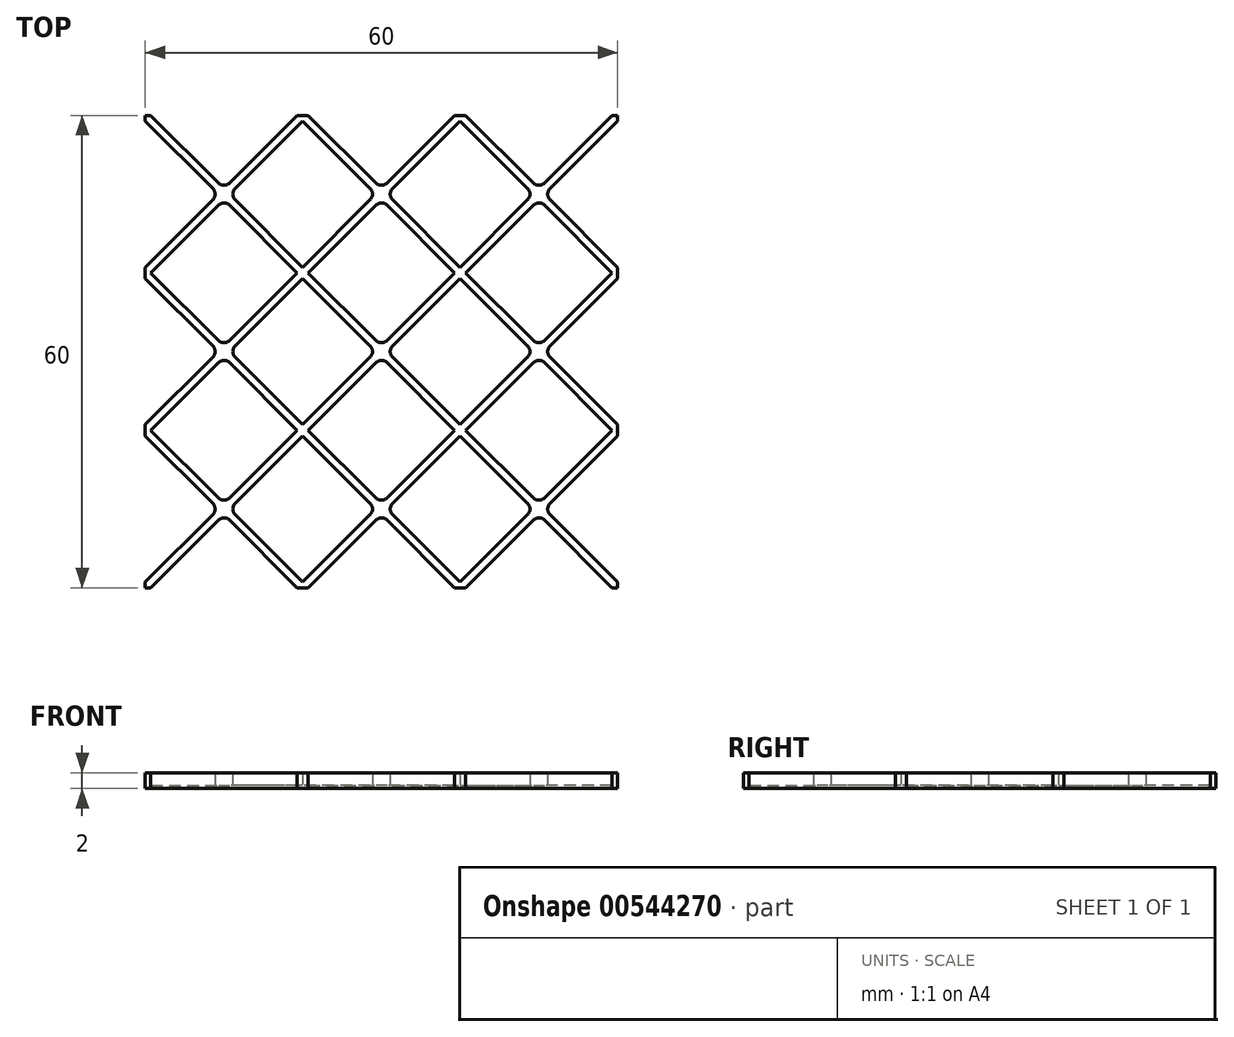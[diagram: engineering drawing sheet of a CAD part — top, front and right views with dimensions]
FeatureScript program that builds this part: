
annotation { "Feature Type Name" : "Feature", "Feature Type Description" : "" }
export const myFeature = defineFeature(function(context is Context, id is Id, definition is map)
    precondition{}
    {
        {
            var Q0;
            Q0=qCreatedBy(makeId("Top.planeOp"),FACE);
            var sketch = newSketch(context, id + "F0", { "sketchPlane" : qUnion([Q0])});
            skLineSegment(sketch, "E0.bottom", {"start": v(10, -10) * mm, "end": v(-10, -10) * mm, "construction": true});
            skLineSegment(sketch, "E0.top", {"start": v(10, 10) * mm, "end": v(-10, 10) * mm, "construction": true});
            skLineSegment(sketch, "E0.left", {"start": v(10, -10) * mm, "end": v(10, 10) * mm, "construction": true});
            skLineSegment(sketch, "E0.right", {"start": v(-10, -10) * mm, "end": v(-10, 10) * mm, "construction": true});
            skPoint(sketch, "E0.middle", {"position": v(0, 0) * mm});
            skLineSegment(sketch, "E1", {"start": v(-10, -10) * mm, "end": v(10, 10) * mm, "construction": true});
            skLineSegment(sketch, "E2", {"start": v(-10, 10) * mm, "end": v(10, -10) * mm, "construction": true});
            skArc(sketch, "E3.0.startCap", {"start": v(-10.35, 9.65) * mm, "mid": v(-10.35, 10.35) * mm, "end": v(-9.65, 10.35) * mm, "construction": true});
            skArc(sketch, "E3.0.endCap", {"start": v(10.35, -9.65) * mm, "mid": v(10.35, -10.35) * mm, "end": v(9.65, -10.35) * mm, "construction": true});
            skLineSegment(sketch, "E3.0.left", {"start": v(-9.65, 10.35) * mm, "end": v(-0.7, 1.41) * mm, "construction": true});
            skLineSegment(sketch, "E3.0.right", {"start": v(-10.35, 9.65) * mm, "end": v(-1.41, 0.7) * mm, "construction": true});
            skArc(sketch, "E3.1.startCap", {"start": v(-9.65, -10.35) * mm, "mid": v(-10.35, -10.35) * mm, "end": v(-10.35, -9.65) * mm, "construction": true});
            skArc(sketch, "E3.1.endCap", {"start": v(9.65, 10.35) * mm, "mid": v(10.35, 10.35) * mm, "end": v(10.35, 9.65) * mm, "construction": true});
            skLineSegment(sketch, "E3.1.left", {"start": v(-10.35, -9.65) * mm, "end": v(-1.41, -0.7) * mm, "construction": true});
            skLineSegment(sketch, "E3.1.right", {"start": v(-9.65, -10.35) * mm, "end": v(-0.7, -1.41) * mm, "construction": true});
            skPoint(sketch, "E4", {"position": v(0, -0.7) * mm});
            skPoint(sketch, "E5", {"position": v(-0.7, 0) * mm});
            skPoint(sketch, "E6", {"position": v(0, 0.7) * mm});
            skPoint(sketch, "E7", {"position": v(0.7, 0) * mm});
            skLineSegment(sketch, "E8", {"start": v(-0.7, 0) * mm, "end": v(-0.7, 0) * mm});
            skLineSegment(sketch, "E9", {"start": v(0.7, 1.41) * mm, "end": v(9.65, 10.35) * mm, "construction": true});
            skLineSegment(sketch, "E10", {"start": v(1.41, -0.7) * mm, "end": v(10.35, -9.65) * mm, "construction": true});
            skLineSegment(sketch, "E11", {"start": v(0, -0.7) * mm, "end": v(0.7, 0) * mm, "construction": true});
            skLineSegment(sketch, "E12", {"start": v(-0.7, 0) * mm, "end": v(0, 0.7) * mm, "construction": true});
            skLineSegment(sketch, "E13", {"start": v(0.7, -1.41) * mm, "end": v(9.65, -10.35) * mm, "construction": true});
            skLineSegment(sketch, "E14", {"start": v(1.41, 0.7) * mm, "end": v(10.35, 9.65) * mm, "construction": true});
            skLineSegment(sketch, "E15", {"start": v(0, 0.7) * mm, "end": v(0.7, 0) * mm, "construction": true});
            skLineSegment(sketch, "E16", {"start": v(-0.7, 0) * mm, "end": v(0, -0.7) * mm, "construction": true});
            skArc(sketch, "E17.filletArc", {"start": v(-1.41, -0.7) * mm, "mid": v(-1.12, 0) * mm, "end": v(-1.41, 0.7) * mm});
            skArc(sketch, "E18.filletArc", {"start": v(-0.7, 1.41) * mm, "mid": v(0, 1.12) * mm, "end": v(0.7, 1.41) * mm});
            skArc(sketch, "E19.filletArc", {"start": v(1.41, 0.7) * mm, "mid": v(1.12, 0) * mm, "end": v(1.41, -0.7) * mm});
            skArc(sketch, "E20.filletArc", {"start": v(0.7, -1.41) * mm, "mid": v(0, -1.12) * mm, "end": v(-0.7, -1.41) * mm});
            skPoint(sketch, "E21", {"position": v(9.3, 10) * mm});
            skPoint(sketch, "E22", {"position": v(10, 9.3) * mm});
            skPoint(sketch, "E23", {"position": v(10, -9.3) * mm});
            skPoint(sketch, "E24", {"position": v(-9.3, -10) * mm});
            skPoint(sketch, "E25", {"position": v(-10, -9.3) * mm});
            skPoint(sketch, "E26", {"position": v(-10, 9.3) * mm});
            skPoint(sketch, "E27", {"position": v(-9.3, 10) * mm});
            skPoint(sketch, "E28", {"position": v(9.3, -10) * mm});
            skLineSegment(sketch, "E29", {"start": v(-1.41, 0.7) * mm, "end": v(-10, 9.3) * mm});
            skLineSegment(sketch, "E30", {"start": v(-10, 9.3) * mm, "end": v(-10, 10) * mm});
            skLineSegment(sketch, "E31", {"start": v(-10, 10) * mm, "end": v(-9.3, 10) * mm});
            skLineSegment(sketch, "E32", {"start": v(-9.3, 10) * mm, "end": v(-0.7, 1.41) * mm});
            skLineSegment(sketch, "E33", {"start": v(0.7, 1.41) * mm, "end": v(9.3, 10) * mm});
            skLineSegment(sketch, "E34", {"start": v(9.3, 10) * mm, "end": v(10, 10) * mm});
            skLineSegment(sketch, "E35", {"start": v(10, 10) * mm, "end": v(10, 9.3) * mm});
            skLineSegment(sketch, "E36", {"start": v(10, 9.3) * mm, "end": v(1.41, 0.7) * mm});
            skLineSegment(sketch, "E37", {"start": v(1.41, -0.7) * mm, "end": v(10, -9.3) * mm});
            skLineSegment(sketch, "E38", {"start": v(10, -9.3) * mm, "end": v(10, -10) * mm});
            skLineSegment(sketch, "E39", {"start": v(10, -10) * mm, "end": v(9.3, -10) * mm});
            skLineSegment(sketch, "E40", {"start": v(9.3, -10) * mm, "end": v(0.7, -1.41) * mm});
            skLineSegment(sketch, "E41", {"start": v(-0.7, -1.41) * mm, "end": v(-9.3, -10) * mm});
            skLineSegment(sketch, "E42", {"start": v(-9.3, -10) * mm, "end": v(-10, -10) * mm});
            skLineSegment(sketch, "E43", {"start": v(-10, -10) * mm, "end": v(-10, -9.3) * mm});
            skLineSegment(sketch, "E44", {"start": v(-10, -9.3) * mm, "end": v(-1.41, -0.7) * mm});
            skLineSegment(sketch, "E45.0.1.0", {"start": v(-10.35, 29.65) * mm, "end": v(-1.41, 20.7) * mm, "construction": true});
            skLineSegment(sketch, "E45.0.1.1", {"start": v(-10, 10) * mm, "end": v(10, 30) * mm, "construction": true});
            skLineSegment(sketch, "E45.0.1.2", {"start": v(0, 20.7) * mm, "end": v(0.7, 20) * mm, "construction": true});
            skPoint(sketch, "E45.0.1.3", {"position": v(9.3, 30) * mm});
            skLineSegment(sketch, "E45.0.1.4", {"start": v(10, 10) * mm, "end": v(10, 30) * mm, "construction": true});
            skLineSegment(sketch, "E45.0.1.5", {"start": v(-10, 10) * mm, "end": v(-10, 30) * mm, "construction": true});
            skArc(sketch, "E45.0.1.6", {"start": v(-10.35, 29.65) * mm, "mid": v(-10.35, 30.35) * mm, "end": v(-9.65, 30.35) * mm, "construction": true});
            skPoint(sketch, "E45.0.1.7", {"position": v(-10, 29.3) * mm});
            skArc(sketch, "E45.0.1.8", {"start": v(10.35, 10.35) * mm, "mid": v(10.35, 9.65) * mm, "end": v(9.65, 9.65) * mm, "construction": true});
            skPoint(sketch, "E45.0.1.10", {"position": v(10, 29.3) * mm});
            skArc(sketch, "E45.0.1.11", {"start": v(1.41, 20.7) * mm, "mid": v(1.12, 20) * mm, "end": v(1.41, 19.3) * mm});
            skLineSegment(sketch, "E45.0.1.12", {"start": v(1.41, 19.3) * mm, "end": v(10.35, 10.35) * mm, "construction": true});
            skPoint(sketch, "E45.0.1.13", {"position": v(0, 20.7) * mm});
            skLineSegment(sketch, "E45.0.1.14", {"start": v(-10.35, 10.35) * mm, "end": v(-1.41, 19.3) * mm, "construction": true});
            skPoint(sketch, "E45.0.1.15", {"position": v(-9.3, 30) * mm});
            skArc(sketch, "E45.0.1.16", {"start": v(-0.7, 21.41) * mm, "mid": v(0, 21.12) * mm, "end": v(0.7, 21.41) * mm});
            skLineSegment(sketch, "E45.0.1.17", {"start": v(0, 19.3) * mm, "end": v(0.7, 20) * mm, "construction": true});
            skLineSegment(sketch, "E45.0.1.18", {"start": v(-0.7, 20) * mm, "end": v(0, 20.7) * mm, "construction": true});
            skLineSegment(sketch, "E45.0.1.19", {"start": v(10, 30) * mm, "end": v(-10, 30) * mm, "construction": true});
            skPoint(sketch, "E45.0.1.20", {"position": v(0, 20) * mm});
            skPoint(sketch, "E45.0.1.22", {"position": v(10, 10.7) * mm});
            skLineSegment(sketch, "E45.0.1.23", {"start": v(-9.65, 30.35) * mm, "end": v(-0.7, 21.41) * mm, "construction": true});
            skLineSegment(sketch, "E45.0.1.24", {"start": v(0.7, 21.41) * mm, "end": v(9.65, 30.35) * mm, "construction": true});
            skLineSegment(sketch, "E45.0.1.25", {"start": v(-10, 30) * mm, "end": v(10, 10) * mm, "construction": true});
            skArc(sketch, "E45.0.1.26", {"start": v(-9.65, 9.65) * mm, "mid": v(-10.35, 9.65) * mm, "end": v(-10.35, 10.35) * mm, "construction": true});
            skLineSegment(sketch, "E45.0.1.27", {"start": v(-0.7, 20) * mm, "end": v(0, 19.3) * mm, "construction": true});
            skArc(sketch, "E45.0.1.28", {"start": v(9.65, 30.35) * mm, "mid": v(10.35, 30.35) * mm, "end": v(10.35, 29.65) * mm, "construction": true});
            skLineSegment(sketch, "E45.0.1.29", {"start": v(-9.65, 9.65) * mm, "end": v(-0.7, 18.59) * mm, "construction": true});
            skPoint(sketch, "E45.0.1.30", {"position": v(0.7, 20) * mm});
            skArc(sketch, "E45.0.1.32", {"start": v(0.7, 18.59) * mm, "mid": v(0, 18.88) * mm, "end": v(-0.7, 18.59) * mm});
            skArc(sketch, "E45.0.1.33", {"start": v(-1.41, 19.3) * mm, "mid": v(-1.12, 20) * mm, "end": v(-1.41, 20.7) * mm});
            skPoint(sketch, "E45.0.1.34", {"position": v(0, 19.3) * mm});
            skLineSegment(sketch, "E45.0.1.35", {"start": v(1.41, 20.7) * mm, "end": v(10.35, 29.65) * mm, "construction": true});
            skPoint(sketch, "E45.0.1.36", {"position": v(-10, 10.7) * mm});
            skLineSegment(sketch, "E45.0.1.37", {"start": v(0.7, 18.59) * mm, "end": v(9.65, 9.65) * mm, "construction": true});
            skPoint(sketch, "E45.0.1.38", {"position": v(0, 19.3) * mm});
            skLineSegment(sketch, "E45.0.1.39", {"start": v(0.7, 21.41) * mm, "end": v(9.3, 30) * mm});
            skLineSegment(sketch, "E45.0.1.40", {"start": v(10, 10) * mm, "end": v(9.3, 10) * mm});
            skLineSegment(sketch, "E45.0.1.41", {"start": v(-10, 29.3) * mm, "end": v(-10, 30) * mm});
            skLineSegment(sketch, "E45.0.1.42", {"start": v(-9.3, 30) * mm, "end": v(-0.7, 21.41) * mm});
            skLineSegment(sketch, "E45.0.1.43", {"start": v(10, 29.3) * mm, "end": v(1.41, 20.7) * mm});
            skLineSegment(sketch, "E45.0.1.44", {"start": v(-10, 30) * mm, "end": v(-9.3, 30) * mm});
            skLineSegment(sketch, "E45.0.1.45", {"start": v(9.3, 10) * mm, "end": v(0.7, 18.59) * mm});
            skLineSegment(sketch, "E45.0.1.46", {"start": v(-9.3, 10) * mm, "end": v(-10, 10) * mm});
            skPoint(sketch, "E45.0.1.47", {"position": v(-0.7, 20) * mm});
            skLineSegment(sketch, "E45.0.1.48", {"start": v(10, 30) * mm, "end": v(10, 29.3) * mm});
            skPoint(sketch, "E45.0.1.49", {"position": v(0, 20.7) * mm});
            skLineSegment(sketch, "E45.0.1.50", {"start": v(-10, 10) * mm, "end": v(-10, 10.7) * mm});
            skLineSegment(sketch, "E45.0.1.51", {"start": v(10, 10.7) * mm, "end": v(10, 10) * mm});
            skLineSegment(sketch, "E45.0.1.52", {"start": v(1.41, 19.3) * mm, "end": v(10, 10.7) * mm});
            skPoint(sketch, "E45.0.1.53", {"position": v(0.7, 20) * mm});
            skLineSegment(sketch, "E45.0.1.54", {"start": v(-10, 10.7) * mm, "end": v(-1.41, 19.3) * mm});
            skLineSegment(sketch, "E45.0.1.55", {"start": v(-1.41, 20.7) * mm, "end": v(-10, 29.3) * mm});
            skLineSegment(sketch, "E45.0.1.56", {"start": v(-0.7, 18.59) * mm, "end": v(-9.3, 10) * mm});
            skLineSegment(sketch, "E45.0.1.57", {"start": v(9.3, 30) * mm, "end": v(10, 30) * mm});
            skPoint(sketch, "E45.0.1.58", {"position": v(-0.7, 20) * mm});
            skLineSegment(sketch, "E45.0.2.0", {"start": v(-10.35, 49.65) * mm, "end": v(-1.41, 40.7) * mm, "construction": true});
            skLineSegment(sketch, "E45.0.2.1", {"start": v(-10, 30) * mm, "end": v(10, 50) * mm, "construction": true});
            skLineSegment(sketch, "E45.0.2.2", {"start": v(0, 40.7) * mm, "end": v(0.7, 40) * mm, "construction": true});
            skPoint(sketch, "E45.0.2.3", {"position": v(9.3, 50) * mm});
            skLineSegment(sketch, "E45.0.2.4", {"start": v(10, 30) * mm, "end": v(10, 50) * mm, "construction": true});
            skLineSegment(sketch, "E45.0.2.5", {"start": v(-10, 30) * mm, "end": v(-10, 50) * mm, "construction": true});
            skArc(sketch, "E45.0.2.6", {"start": v(-10.35, 49.65) * mm, "mid": v(-10.35, 50.35) * mm, "end": v(-9.65, 50.35) * mm, "construction": true});
            skPoint(sketch, "E45.0.2.7", {"position": v(-10, 49.3) * mm});
            skArc(sketch, "E45.0.2.8", {"start": v(10.35, 30.35) * mm, "mid": v(10.35, 29.65) * mm, "end": v(9.65, 29.65) * mm, "construction": true});
            skPoint(sketch, "E45.0.2.9", {"position": v(9.3, 30) * mm});
            skPoint(sketch, "E45.0.2.10", {"position": v(10, 49.3) * mm});
            skArc(sketch, "E45.0.2.11", {"start": v(1.41, 40.7) * mm, "mid": v(1.12, 40) * mm, "end": v(1.41, 39.3) * mm});
            skLineSegment(sketch, "E45.0.2.12", {"start": v(1.41, 39.3) * mm, "end": v(10.35, 30.35) * mm, "construction": true});
            skPoint(sketch, "E45.0.2.13", {"position": v(0, 40.7) * mm});
            skLineSegment(sketch, "E45.0.2.14", {"start": v(-10.35, 30.35) * mm, "end": v(-1.41, 39.3) * mm, "construction": true});
            skPoint(sketch, "E45.0.2.15", {"position": v(-9.3, 50) * mm});
            skArc(sketch, "E45.0.2.16", {"start": v(-0.7, 41.41) * mm, "mid": v(0, 41.12) * mm, "end": v(0.7, 41.41) * mm});
            skLineSegment(sketch, "E45.0.2.17", {"start": v(0, 39.3) * mm, "end": v(0.7, 40) * mm, "construction": true});
            skLineSegment(sketch, "E45.0.2.18", {"start": v(-0.7, 40) * mm, "end": v(0, 40.7) * mm, "construction": true});
            skLineSegment(sketch, "E45.0.2.19", {"start": v(10, 50) * mm, "end": v(-10, 50) * mm, "construction": true});
            skPoint(sketch, "E45.0.2.20", {"position": v(0, 40) * mm});
            skLineSegment(sketch, "E45.0.2.21", {"start": v(10, 30) * mm, "end": v(-10, 30) * mm, "construction": true});
            skPoint(sketch, "E45.0.2.22", {"position": v(10, 30.7) * mm});
            skLineSegment(sketch, "E45.0.2.23", {"start": v(-9.65, 50.35) * mm, "end": v(-0.7, 41.41) * mm, "construction": true});
            skLineSegment(sketch, "E45.0.2.24", {"start": v(0.7, 41.41) * mm, "end": v(9.65, 50.35) * mm, "construction": true});
            skLineSegment(sketch, "E45.0.2.25", {"start": v(-10, 50) * mm, "end": v(10, 30) * mm, "construction": true});
            skArc(sketch, "E45.0.2.26", {"start": v(-9.65, 29.65) * mm, "mid": v(-10.35, 29.65) * mm, "end": v(-10.35, 30.35) * mm, "construction": true});
            skLineSegment(sketch, "E45.0.2.27", {"start": v(-0.7, 40) * mm, "end": v(0, 39.3) * mm, "construction": true});
            skArc(sketch, "E45.0.2.28", {"start": v(9.65, 50.35) * mm, "mid": v(10.35, 50.35) * mm, "end": v(10.35, 49.65) * mm, "construction": true});
            skLineSegment(sketch, "E45.0.2.29", {"start": v(-9.65, 29.65) * mm, "end": v(-0.7, 38.59) * mm, "construction": true});
            skPoint(sketch, "E45.0.2.30", {"position": v(0.7, 40) * mm});
            skPoint(sketch, "E45.0.2.31", {"position": v(-9.3, 30) * mm});
            skArc(sketch, "E45.0.2.32", {"start": v(0.7, 38.59) * mm, "mid": v(0, 38.88) * mm, "end": v(-0.7, 38.59) * mm});
            skArc(sketch, "E45.0.2.33", {"start": v(-1.41, 39.3) * mm, "mid": v(-1.12, 40) * mm, "end": v(-1.41, 40.7) * mm});
            skPoint(sketch, "E45.0.2.34", {"position": v(0, 39.3) * mm});
            skLineSegment(sketch, "E45.0.2.35", {"start": v(1.41, 40.7) * mm, "end": v(10.35, 49.65) * mm, "construction": true});
            skPoint(sketch, "E45.0.2.36", {"position": v(-10, 30.7) * mm});
            skLineSegment(sketch, "E45.0.2.37", {"start": v(0.7, 38.59) * mm, "end": v(9.65, 29.65) * mm, "construction": true});
            skPoint(sketch, "E45.0.2.38", {"position": v(0, 39.3) * mm});
            skLineSegment(sketch, "E45.0.2.39", {"start": v(0.7, 41.41) * mm, "end": v(9.3, 50) * mm});
            skLineSegment(sketch, "E45.0.2.40", {"start": v(10, 30) * mm, "end": v(9.3, 30) * mm});
            skLineSegment(sketch, "E45.0.2.41", {"start": v(-10, 49.3) * mm, "end": v(-10, 50) * mm});
            skLineSegment(sketch, "E45.0.2.42", {"start": v(-9.3, 50) * mm, "end": v(-0.7, 41.41) * mm});
            skLineSegment(sketch, "E45.0.2.43", {"start": v(10, 49.3) * mm, "end": v(1.41, 40.7) * mm});
            skLineSegment(sketch, "E45.0.2.44", {"start": v(-10, 50) * mm, "end": v(-9.3, 50) * mm});
            skLineSegment(sketch, "E45.0.2.45", {"start": v(9.3, 30) * mm, "end": v(0.7, 38.59) * mm});
            skLineSegment(sketch, "E45.0.2.46", {"start": v(-9.3, 30) * mm, "end": v(-10, 30) * mm});
            skPoint(sketch, "E45.0.2.47", {"position": v(-0.7, 40) * mm});
            skLineSegment(sketch, "E45.0.2.48", {"start": v(10, 50) * mm, "end": v(10, 49.3) * mm});
            skPoint(sketch, "E45.0.2.49", {"position": v(0, 40.7) * mm});
            skLineSegment(sketch, "E45.0.2.50", {"start": v(-10, 30) * mm, "end": v(-10, 30.7) * mm});
            skLineSegment(sketch, "E45.0.2.51", {"start": v(10, 30.7) * mm, "end": v(10, 30) * mm});
            skLineSegment(sketch, "E45.0.2.52", {"start": v(1.41, 39.3) * mm, "end": v(10, 30.7) * mm});
            skPoint(sketch, "E45.0.2.53", {"position": v(0.7, 40) * mm});
            skLineSegment(sketch, "E45.0.2.54", {"start": v(-10, 30.7) * mm, "end": v(-1.41, 39.3) * mm});
            skLineSegment(sketch, "E45.0.2.55", {"start": v(-1.41, 40.7) * mm, "end": v(-10, 49.3) * mm});
            skLineSegment(sketch, "E45.0.2.56", {"start": v(-0.7, 38.59) * mm, "end": v(-9.3, 30) * mm});
            skLineSegment(sketch, "E45.0.2.57", {"start": v(9.3, 50) * mm, "end": v(10, 50) * mm});
            skPoint(sketch, "E45.0.2.58", {"position": v(-0.7, 40) * mm});
            skLineSegment(sketch, "E45.1.0.0", {"start": v(9.65, 9.65) * mm, "end": v(18.59, 0.7) * mm, "construction": true});
            skLineSegment(sketch, "E45.1.0.1", {"start": v(10, -10) * mm, "end": v(30, 10) * mm, "construction": true});
            skLineSegment(sketch, "E45.1.0.2", {"start": v(20, 0.7) * mm, "end": v(20.7, 0) * mm, "construction": true});
            skPoint(sketch, "E45.1.0.3", {"position": v(29.3, 10) * mm});
            skLineSegment(sketch, "E45.1.0.4", {"start": v(30, -10) * mm, "end": v(30, 10) * mm, "construction": true});
            skArc(sketch, "E45.1.0.6", {"start": v(9.65, 9.65) * mm, "mid": v(9.65, 10.35) * mm, "end": v(10.35, 10.35) * mm, "construction": true});
            skArc(sketch, "E45.1.0.8", {"start": v(30.35, -9.65) * mm, "mid": v(30.35, -10.35) * mm, "end": v(29.65, -10.35) * mm, "construction": true});
            skPoint(sketch, "E45.1.0.9", {"position": v(29.3, -10) * mm});
            skPoint(sketch, "E45.1.0.10", {"position": v(30, 9.3) * mm});
            skArc(sketch, "E45.1.0.11", {"start": v(21.41, 0.7) * mm, "mid": v(21.12, 0) * mm, "end": v(21.41, -0.7) * mm});
            skLineSegment(sketch, "E45.1.0.12", {"start": v(21.41, -0.7) * mm, "end": v(30.35, -9.65) * mm, "construction": true});
            skPoint(sketch, "E45.1.0.13", {"position": v(20, 0.7) * mm});
            skLineSegment(sketch, "E45.1.0.14", {"start": v(9.65, -9.65) * mm, "end": v(18.59, -0.7) * mm, "construction": true});
            skPoint(sketch, "E45.1.0.15", {"position": v(10.7, 10) * mm});
            skArc(sketch, "E45.1.0.16", {"start": v(19.3, 1.41) * mm, "mid": v(20, 1.12) * mm, "end": v(20.7, 1.41) * mm});
            skLineSegment(sketch, "E45.1.0.17", {"start": v(20, -0.7) * mm, "end": v(20.7, 0) * mm, "construction": true});
            skLineSegment(sketch, "E45.1.0.18", {"start": v(19.3, 0) * mm, "end": v(20, 0.7) * mm, "construction": true});
            skLineSegment(sketch, "E45.1.0.19", {"start": v(30, 10) * mm, "end": v(10, 10) * mm, "construction": true});
            skPoint(sketch, "E45.1.0.20", {"position": v(20, 0) * mm});
            skLineSegment(sketch, "E45.1.0.21", {"start": v(30, -10) * mm, "end": v(10, -10) * mm, "construction": true});
            skPoint(sketch, "E45.1.0.22", {"position": v(30, -9.3) * mm});
            skLineSegment(sketch, "E45.1.0.23", {"start": v(10.35, 10.35) * mm, "end": v(19.3, 1.41) * mm, "construction": true});
            skLineSegment(sketch, "E45.1.0.24", {"start": v(20.7, 1.41) * mm, "end": v(29.65, 10.35) * mm, "construction": true});
            skLineSegment(sketch, "E45.1.0.25", {"start": v(10, 10) * mm, "end": v(30, -10) * mm, "construction": true});
            skArc(sketch, "E45.1.0.26", {"start": v(10.35, -10.35) * mm, "mid": v(9.65, -10.35) * mm, "end": v(9.65, -9.65) * mm, "construction": true});
            skLineSegment(sketch, "E45.1.0.27", {"start": v(19.3, 0) * mm, "end": v(20, -0.7) * mm, "construction": true});
            skArc(sketch, "E45.1.0.28", {"start": v(29.65, 10.35) * mm, "mid": v(30.35, 10.35) * mm, "end": v(30.35, 9.65) * mm, "construction": true});
            skLineSegment(sketch, "E45.1.0.29", {"start": v(10.35, -10.35) * mm, "end": v(19.3, -1.41) * mm, "construction": true});
            skPoint(sketch, "E45.1.0.30", {"position": v(20.7, 0) * mm});
            skPoint(sketch, "E45.1.0.31", {"position": v(10.7, -10) * mm});
            skArc(sketch, "E45.1.0.32", {"start": v(20.7, -1.41) * mm, "mid": v(20, -1.12) * mm, "end": v(19.3, -1.41) * mm});
            skArc(sketch, "E45.1.0.33", {"start": v(18.59, -0.7) * mm, "mid": v(18.88, 0) * mm, "end": v(18.59, 0.7) * mm});
            skPoint(sketch, "E45.1.0.34", {"position": v(20, -0.7) * mm});
            skLineSegment(sketch, "E45.1.0.35", {"start": v(21.41, 0.7) * mm, "end": v(30.35, 9.65) * mm, "construction": true});
            skLineSegment(sketch, "E45.1.0.37", {"start": v(20.7, -1.41) * mm, "end": v(29.65, -10.35) * mm, "construction": true});
            skPoint(sketch, "E45.1.0.38", {"position": v(20, -0.7) * mm});
            skLineSegment(sketch, "E45.1.0.39", {"start": v(20.7, 1.41) * mm, "end": v(29.3, 10) * mm});
            skLineSegment(sketch, "E45.1.0.40", {"start": v(30, -10) * mm, "end": v(29.3, -10) * mm});
            skLineSegment(sketch, "E45.1.0.41", {"start": v(10, 9.3) * mm, "end": v(10, 10) * mm});
            skLineSegment(sketch, "E45.1.0.42", {"start": v(10.7, 10) * mm, "end": v(19.3, 1.41) * mm});
            skLineSegment(sketch, "E45.1.0.43", {"start": v(30, 9.3) * mm, "end": v(21.41, 0.7) * mm});
            skLineSegment(sketch, "E45.1.0.44", {"start": v(10, 10) * mm, "end": v(10.7, 10) * mm});
            skLineSegment(sketch, "E45.1.0.45", {"start": v(29.3, -10) * mm, "end": v(20.7, -1.41) * mm});
            skLineSegment(sketch, "E45.1.0.46", {"start": v(10.7, -10) * mm, "end": v(10, -10) * mm});
            skPoint(sketch, "E45.1.0.47", {"position": v(19.3, 0) * mm});
            skLineSegment(sketch, "E45.1.0.48", {"start": v(30, 10) * mm, "end": v(30, 9.3) * mm});
            skPoint(sketch, "E45.1.0.49", {"position": v(20, 0.7) * mm});
            skLineSegment(sketch, "E45.1.0.50", {"start": v(10, -10) * mm, "end": v(10, -9.3) * mm});
            skLineSegment(sketch, "E45.1.0.51", {"start": v(30, -9.3) * mm, "end": v(30, -10) * mm});
            skLineSegment(sketch, "E45.1.0.52", {"start": v(21.41, -0.7) * mm, "end": v(30, -9.3) * mm});
            skPoint(sketch, "E45.1.0.53", {"position": v(20.7, 0) * mm});
            skLineSegment(sketch, "E45.1.0.54", {"start": v(10, -9.3) * mm, "end": v(18.59, -0.7) * mm});
            skLineSegment(sketch, "E45.1.0.55", {"start": v(18.59, 0.7) * mm, "end": v(10, 9.3) * mm});
            skLineSegment(sketch, "E45.1.0.56", {"start": v(19.3, -1.41) * mm, "end": v(10.7, -10) * mm});
            skLineSegment(sketch, "E45.1.0.57", {"start": v(29.3, 10) * mm, "end": v(30, 10) * mm});
            skPoint(sketch, "E45.1.0.58", {"position": v(19.3, 0) * mm});
            skLineSegment(sketch, "E45.1.1.0", {"start": v(9.65, 29.65) * mm, "end": v(18.59, 20.7) * mm, "construction": true});
            skLineSegment(sketch, "E45.1.1.1", {"start": v(10, 10) * mm, "end": v(30, 30) * mm, "construction": true});
            skLineSegment(sketch, "E45.1.1.2", {"start": v(20, 20.7) * mm, "end": v(20.7, 20) * mm, "construction": true});
            skPoint(sketch, "E45.1.1.3", {"position": v(29.3, 30) * mm});
            skLineSegment(sketch, "E45.1.1.4", {"start": v(30, 10) * mm, "end": v(30, 30) * mm, "construction": true});
            skLineSegment(sketch, "E45.1.1.5", {"start": v(10, 10) * mm, "end": v(10, 30) * mm, "construction": true});
            skArc(sketch, "E45.1.1.6", {"start": v(9.65, 29.65) * mm, "mid": v(9.65, 30.35) * mm, "end": v(10.35, 30.35) * mm, "construction": true});
            skPoint(sketch, "E45.1.1.7", {"position": v(10, 29.3) * mm});
            skArc(sketch, "E45.1.1.8", {"start": v(30.35, 10.35) * mm, "mid": v(30.35, 9.65) * mm, "end": v(29.65, 9.65) * mm, "construction": true});
            skPoint(sketch, "E45.1.1.9", {"position": v(29.3, 10) * mm});
            skPoint(sketch, "E45.1.1.10", {"position": v(30, 29.3) * mm});
            skArc(sketch, "E45.1.1.11", {"start": v(21.41, 20.7) * mm, "mid": v(21.12, 20) * mm, "end": v(21.41, 19.3) * mm});
            skLineSegment(sketch, "E45.1.1.12", {"start": v(21.41, 19.3) * mm, "end": v(30.35, 10.35) * mm, "construction": true});
            skPoint(sketch, "E45.1.1.13", {"position": v(20, 20.7) * mm});
            skLineSegment(sketch, "E45.1.1.14", {"start": v(9.65, 10.35) * mm, "end": v(18.59, 19.3) * mm, "construction": true});
            skPoint(sketch, "E45.1.1.15", {"position": v(10.7, 30) * mm});
            skArc(sketch, "E45.1.1.16", {"start": v(19.3, 21.41) * mm, "mid": v(20, 21.12) * mm, "end": v(20.7, 21.41) * mm});
            skLineSegment(sketch, "E45.1.1.17", {"start": v(20, 19.3) * mm, "end": v(20.7, 20) * mm, "construction": true});
            skLineSegment(sketch, "E45.1.1.18", {"start": v(19.3, 20) * mm, "end": v(20, 20.7) * mm, "construction": true});
            skLineSegment(sketch, "E45.1.1.19", {"start": v(30, 30) * mm, "end": v(10, 30) * mm, "construction": true});
            skPoint(sketch, "E45.1.1.20", {"position": v(20, 20) * mm});
            skLineSegment(sketch, "E45.1.1.21", {"start": v(30, 10) * mm, "end": v(10, 10) * mm, "construction": true});
            skPoint(sketch, "E45.1.1.22", {"position": v(30, 10.7) * mm});
            skLineSegment(sketch, "E45.1.1.23", {"start": v(10.35, 30.35) * mm, "end": v(19.3, 21.41) * mm, "construction": true});
            skLineSegment(sketch, "E45.1.1.24", {"start": v(20.7, 21.41) * mm, "end": v(29.65, 30.35) * mm, "construction": true});
            skLineSegment(sketch, "E45.1.1.25", {"start": v(10, 30) * mm, "end": v(30, 10) * mm, "construction": true});
            skArc(sketch, "E45.1.1.26", {"start": v(10.35, 9.65) * mm, "mid": v(9.65, 9.65) * mm, "end": v(9.65, 10.35) * mm, "construction": true});
            skLineSegment(sketch, "E45.1.1.27", {"start": v(19.3, 20) * mm, "end": v(20, 19.3) * mm, "construction": true});
            skArc(sketch, "E45.1.1.28", {"start": v(29.65, 30.35) * mm, "mid": v(30.35, 30.35) * mm, "end": v(30.35, 29.65) * mm, "construction": true});
            skLineSegment(sketch, "E45.1.1.29", {"start": v(10.35, 9.65) * mm, "end": v(19.3, 18.59) * mm, "construction": true});
            skPoint(sketch, "E45.1.1.30", {"position": v(20.7, 20) * mm});
            skPoint(sketch, "E45.1.1.31", {"position": v(10.7, 10) * mm});
            skArc(sketch, "E45.1.1.32", {"start": v(20.7, 18.59) * mm, "mid": v(20, 18.88) * mm, "end": v(19.3, 18.59) * mm});
            skArc(sketch, "E45.1.1.33", {"start": v(18.59, 19.3) * mm, "mid": v(18.88, 20) * mm, "end": v(18.59, 20.7) * mm});
            skPoint(sketch, "E45.1.1.34", {"position": v(20, 19.3) * mm});
            skLineSegment(sketch, "E45.1.1.35", {"start": v(21.41, 20.7) * mm, "end": v(30.35, 29.65) * mm, "construction": true});
            skPoint(sketch, "E45.1.1.36", {"position": v(10, 10.7) * mm});
            skLineSegment(sketch, "E45.1.1.37", {"start": v(20.7, 18.59) * mm, "end": v(29.65, 9.65) * mm, "construction": true});
            skPoint(sketch, "E45.1.1.38", {"position": v(20, 19.3) * mm});
            skLineSegment(sketch, "E45.1.1.39", {"start": v(20.7, 21.41) * mm, "end": v(29.3, 30) * mm});
            skLineSegment(sketch, "E45.1.1.40", {"start": v(30, 10) * mm, "end": v(29.3, 10) * mm});
            skLineSegment(sketch, "E45.1.1.41", {"start": v(10, 29.3) * mm, "end": v(10, 30) * mm});
            skLineSegment(sketch, "E45.1.1.42", {"start": v(10.7, 30) * mm, "end": v(19.3, 21.41) * mm});
            skLineSegment(sketch, "E45.1.1.43", {"start": v(30, 29.3) * mm, "end": v(21.41, 20.7) * mm});
            skLineSegment(sketch, "E45.1.1.44", {"start": v(10, 30) * mm, "end": v(10.7, 30) * mm});
            skLineSegment(sketch, "E45.1.1.45", {"start": v(29.3, 10) * mm, "end": v(20.7, 18.59) * mm});
            skLineSegment(sketch, "E45.1.1.46", {"start": v(10.7, 10) * mm, "end": v(10, 10) * mm});
            skPoint(sketch, "E45.1.1.47", {"position": v(19.3, 20) * mm});
            skLineSegment(sketch, "E45.1.1.48", {"start": v(30, 30) * mm, "end": v(30, 29.3) * mm});
            skPoint(sketch, "E45.1.1.49", {"position": v(20, 20.7) * mm});
            skLineSegment(sketch, "E45.1.1.50", {"start": v(10, 10) * mm, "end": v(10, 10.7) * mm});
            skLineSegment(sketch, "E45.1.1.51", {"start": v(30, 10.7) * mm, "end": v(30, 10) * mm});
            skLineSegment(sketch, "E45.1.1.52", {"start": v(21.41, 19.3) * mm, "end": v(30, 10.7) * mm});
            skPoint(sketch, "E45.1.1.53", {"position": v(20.7, 20) * mm});
            skLineSegment(sketch, "E45.1.1.54", {"start": v(10, 10.7) * mm, "end": v(18.59, 19.3) * mm});
            skLineSegment(sketch, "E45.1.1.55", {"start": v(18.59, 20.7) * mm, "end": v(10, 29.3) * mm});
            skLineSegment(sketch, "E45.1.1.56", {"start": v(19.3, 18.59) * mm, "end": v(10.7, 10) * mm});
            skLineSegment(sketch, "E45.1.1.57", {"start": v(29.3, 30) * mm, "end": v(30, 30) * mm});
            skPoint(sketch, "E45.1.1.58", {"position": v(19.3, 20) * mm});
            skLineSegment(sketch, "E45.1.2.0", {"start": v(9.65, 49.65) * mm, "end": v(18.59, 40.7) * mm, "construction": true});
            skLineSegment(sketch, "E45.1.2.1", {"start": v(10, 30) * mm, "end": v(30, 50) * mm, "construction": true});
            skLineSegment(sketch, "E45.1.2.2", {"start": v(20, 40.7) * mm, "end": v(20.7, 40) * mm, "construction": true});
            skPoint(sketch, "E45.1.2.3", {"position": v(29.3, 50) * mm});
            skLineSegment(sketch, "E45.1.2.4", {"start": v(30, 30) * mm, "end": v(30, 50) * mm, "construction": true});
            skLineSegment(sketch, "E45.1.2.5", {"start": v(10, 30) * mm, "end": v(10, 50) * mm, "construction": true});
            skArc(sketch, "E45.1.2.6", {"start": v(9.65, 49.65) * mm, "mid": v(9.65, 50.35) * mm, "end": v(10.35, 50.35) * mm, "construction": true});
            skPoint(sketch, "E45.1.2.7", {"position": v(10, 49.3) * mm});
            skArc(sketch, "E45.1.2.8", {"start": v(30.35, 30.35) * mm, "mid": v(30.35, 29.65) * mm, "end": v(29.65, 29.65) * mm, "construction": true});
            skPoint(sketch, "E45.1.2.9", {"position": v(29.3, 30) * mm});
            skPoint(sketch, "E45.1.2.10", {"position": v(30, 49.3) * mm});
            skArc(sketch, "E45.1.2.11", {"start": v(21.41, 40.7) * mm, "mid": v(21.12, 40) * mm, "end": v(21.41, 39.3) * mm});
            skLineSegment(sketch, "E45.1.2.12", {"start": v(21.41, 39.3) * mm, "end": v(30.35, 30.35) * mm, "construction": true});
            skPoint(sketch, "E45.1.2.13", {"position": v(20, 40.7) * mm});
            skLineSegment(sketch, "E45.1.2.14", {"start": v(9.65, 30.35) * mm, "end": v(18.59, 39.3) * mm, "construction": true});
            skPoint(sketch, "E45.1.2.15", {"position": v(10.7, 50) * mm});
            skArc(sketch, "E45.1.2.16", {"start": v(19.3, 41.41) * mm, "mid": v(20, 41.12) * mm, "end": v(20.7, 41.41) * mm});
            skLineSegment(sketch, "E45.1.2.17", {"start": v(20, 39.3) * mm, "end": v(20.7, 40) * mm, "construction": true});
            skLineSegment(sketch, "E45.1.2.18", {"start": v(19.3, 40) * mm, "end": v(20, 40.7) * mm, "construction": true});
            skLineSegment(sketch, "E45.1.2.19", {"start": v(30, 50) * mm, "end": v(10, 50) * mm, "construction": true});
            skPoint(sketch, "E45.1.2.20", {"position": v(20, 40) * mm});
            skLineSegment(sketch, "E45.1.2.21", {"start": v(30, 30) * mm, "end": v(10, 30) * mm, "construction": true});
            skPoint(sketch, "E45.1.2.22", {"position": v(30, 30.7) * mm});
            skLineSegment(sketch, "E45.1.2.23", {"start": v(10.35, 50.35) * mm, "end": v(19.3, 41.41) * mm, "construction": true});
            skLineSegment(sketch, "E45.1.2.24", {"start": v(20.7, 41.41) * mm, "end": v(29.65, 50.35) * mm, "construction": true});
            skLineSegment(sketch, "E45.1.2.25", {"start": v(10, 50) * mm, "end": v(30, 30) * mm, "construction": true});
            skArc(sketch, "E45.1.2.26", {"start": v(10.35, 29.65) * mm, "mid": v(9.65, 29.65) * mm, "end": v(9.65, 30.35) * mm, "construction": true});
            skLineSegment(sketch, "E45.1.2.27", {"start": v(19.3, 40) * mm, "end": v(20, 39.3) * mm, "construction": true});
            skArc(sketch, "E45.1.2.28", {"start": v(29.65, 50.35) * mm, "mid": v(30.35, 50.35) * mm, "end": v(30.35, 49.65) * mm, "construction": true});
            skLineSegment(sketch, "E45.1.2.29", {"start": v(10.35, 29.65) * mm, "end": v(19.3, 38.59) * mm, "construction": true});
            skPoint(sketch, "E45.1.2.30", {"position": v(20.7, 40) * mm});
            skPoint(sketch, "E45.1.2.31", {"position": v(10.7, 30) * mm});
            skArc(sketch, "E45.1.2.32", {"start": v(20.7, 38.59) * mm, "mid": v(20, 38.88) * mm, "end": v(19.3, 38.59) * mm});
            skArc(sketch, "E45.1.2.33", {"start": v(18.59, 39.3) * mm, "mid": v(18.88, 40) * mm, "end": v(18.59, 40.7) * mm});
            skPoint(sketch, "E45.1.2.34", {"position": v(20, 39.3) * mm});
            skLineSegment(sketch, "E45.1.2.35", {"start": v(21.41, 40.7) * mm, "end": v(30.35, 49.65) * mm, "construction": true});
            skPoint(sketch, "E45.1.2.36", {"position": v(10, 30.7) * mm});
            skLineSegment(sketch, "E45.1.2.37", {"start": v(20.7, 38.59) * mm, "end": v(29.65, 29.65) * mm, "construction": true});
            skPoint(sketch, "E45.1.2.38", {"position": v(20, 39.3) * mm});
            skLineSegment(sketch, "E45.1.2.39", {"start": v(20.7, 41.41) * mm, "end": v(29.3, 50) * mm});
            skLineSegment(sketch, "E45.1.2.40", {"start": v(30, 30) * mm, "end": v(29.3, 30) * mm});
            skLineSegment(sketch, "E45.1.2.41", {"start": v(10, 49.3) * mm, "end": v(10, 50) * mm});
            skLineSegment(sketch, "E45.1.2.42", {"start": v(10.7, 50) * mm, "end": v(19.3, 41.41) * mm});
            skLineSegment(sketch, "E45.1.2.43", {"start": v(30, 49.3) * mm, "end": v(21.41, 40.7) * mm});
            skLineSegment(sketch, "E45.1.2.44", {"start": v(10, 50) * mm, "end": v(10.7, 50) * mm});
            skLineSegment(sketch, "E45.1.2.45", {"start": v(29.3, 30) * mm, "end": v(20.7, 38.59) * mm});
            skLineSegment(sketch, "E45.1.2.46", {"start": v(10.7, 30) * mm, "end": v(10, 30) * mm});
            skPoint(sketch, "E45.1.2.47", {"position": v(19.3, 40) * mm});
            skLineSegment(sketch, "E45.1.2.48", {"start": v(30, 50) * mm, "end": v(30, 49.3) * mm});
            skPoint(sketch, "E45.1.2.49", {"position": v(20, 40.7) * mm});
            skLineSegment(sketch, "E45.1.2.50", {"start": v(10, 30) * mm, "end": v(10, 30.7) * mm});
            skLineSegment(sketch, "E45.1.2.51", {"start": v(30, 30.7) * mm, "end": v(30, 30) * mm});
            skLineSegment(sketch, "E45.1.2.52", {"start": v(21.41, 39.3) * mm, "end": v(30, 30.7) * mm});
            skPoint(sketch, "E45.1.2.53", {"position": v(20.7, 40) * mm});
            skLineSegment(sketch, "E45.1.2.54", {"start": v(10, 30.7) * mm, "end": v(18.59, 39.3) * mm});
            skLineSegment(sketch, "E45.1.2.55", {"start": v(18.59, 40.7) * mm, "end": v(10, 49.3) * mm});
            skLineSegment(sketch, "E45.1.2.56", {"start": v(19.3, 38.59) * mm, "end": v(10.7, 30) * mm});
            skLineSegment(sketch, "E45.1.2.57", {"start": v(29.3, 50) * mm, "end": v(30, 50) * mm});
            skPoint(sketch, "E45.1.2.58", {"position": v(19.3, 40) * mm});
            skLineSegment(sketch, "E45.2.0.0", {"start": v(29.65, 9.65) * mm, "end": v(38.59, 0.7) * mm, "construction": true});
            skLineSegment(sketch, "E45.2.0.1", {"start": v(30, -10) * mm, "end": v(50, 10) * mm, "construction": true});
            skLineSegment(sketch, "E45.2.0.2", {"start": v(40, 0.7) * mm, "end": v(40.7, 0) * mm, "construction": true});
            skPoint(sketch, "E45.2.0.3", {"position": v(49.3, 10) * mm});
            skLineSegment(sketch, "E45.2.0.4", {"start": v(50, -10) * mm, "end": v(50, 10) * mm, "construction": true});
            skLineSegment(sketch, "E45.2.0.5", {"start": v(30, -10) * mm, "end": v(30, 10) * mm, "construction": true});
            skArc(sketch, "E45.2.0.6", {"start": v(29.65, 9.65) * mm, "mid": v(29.65, 10.35) * mm, "end": v(30.35, 10.35) * mm, "construction": true});
            skPoint(sketch, "E45.2.0.7", {"position": v(30, 9.3) * mm});
            skArc(sketch, "E45.2.0.8", {"start": v(50.35, -9.65) * mm, "mid": v(50.35, -10.35) * mm, "end": v(49.65, -10.35) * mm, "construction": true});
            skPoint(sketch, "E45.2.0.9", {"position": v(49.3, -10) * mm});
            skPoint(sketch, "E45.2.0.10", {"position": v(50, 9.3) * mm});
            skArc(sketch, "E45.2.0.11", {"start": v(41.41, 0.7) * mm, "mid": v(41.12, 0) * mm, "end": v(41.41, -0.7) * mm});
            skLineSegment(sketch, "E45.2.0.12", {"start": v(41.41, -0.7) * mm, "end": v(50.35, -9.65) * mm, "construction": true});
            skPoint(sketch, "E45.2.0.13", {"position": v(40, 0.7) * mm});
            skLineSegment(sketch, "E45.2.0.14", {"start": v(29.65, -9.65) * mm, "end": v(38.59, -0.7) * mm, "construction": true});
            skPoint(sketch, "E45.2.0.15", {"position": v(30.7, 10) * mm});
            skArc(sketch, "E45.2.0.16", {"start": v(39.3, 1.41) * mm, "mid": v(40, 1.12) * mm, "end": v(40.7, 1.41) * mm});
            skLineSegment(sketch, "E45.2.0.17", {"start": v(40, -0.7) * mm, "end": v(40.7, 0) * mm, "construction": true});
            skLineSegment(sketch, "E45.2.0.18", {"start": v(39.3, 0) * mm, "end": v(40, 0.7) * mm, "construction": true});
            skLineSegment(sketch, "E45.2.0.19", {"start": v(50, 10) * mm, "end": v(30, 10) * mm, "construction": true});
            skPoint(sketch, "E45.2.0.20", {"position": v(40, 0) * mm});
            skLineSegment(sketch, "E45.2.0.21", {"start": v(50, -10) * mm, "end": v(30, -10) * mm, "construction": true});
            skPoint(sketch, "E45.2.0.22", {"position": v(50, -9.3) * mm});
            skLineSegment(sketch, "E45.2.0.23", {"start": v(30.35, 10.35) * mm, "end": v(39.3, 1.41) * mm, "construction": true});
            skLineSegment(sketch, "E45.2.0.24", {"start": v(40.7, 1.41) * mm, "end": v(49.65, 10.35) * mm, "construction": true});
            skLineSegment(sketch, "E45.2.0.25", {"start": v(30, 10) * mm, "end": v(50, -10) * mm, "construction": true});
            skArc(sketch, "E45.2.0.26", {"start": v(30.35, -10.35) * mm, "mid": v(29.65, -10.35) * mm, "end": v(29.65, -9.65) * mm, "construction": true});
            skLineSegment(sketch, "E45.2.0.27", {"start": v(39.3, 0) * mm, "end": v(40, -0.7) * mm, "construction": true});
            skArc(sketch, "E45.2.0.28", {"start": v(49.65, 10.35) * mm, "mid": v(50.35, 10.35) * mm, "end": v(50.35, 9.65) * mm, "construction": true});
            skLineSegment(sketch, "E45.2.0.29", {"start": v(30.35, -10.35) * mm, "end": v(39.3, -1.41) * mm, "construction": true});
            skPoint(sketch, "E45.2.0.30", {"position": v(40.7, 0) * mm});
            skPoint(sketch, "E45.2.0.31", {"position": v(30.7, -10) * mm});
            skArc(sketch, "E45.2.0.32", {"start": v(40.7, -1.41) * mm, "mid": v(40, -1.12) * mm, "end": v(39.3, -1.41) * mm});
            skArc(sketch, "E45.2.0.33", {"start": v(38.59, -0.7) * mm, "mid": v(38.88, 0) * mm, "end": v(38.59, 0.7) * mm});
            skPoint(sketch, "E45.2.0.34", {"position": v(40, -0.7) * mm});
            skLineSegment(sketch, "E45.2.0.35", {"start": v(41.41, 0.7) * mm, "end": v(50.35, 9.65) * mm, "construction": true});
            skPoint(sketch, "E45.2.0.36", {"position": v(30, -9.3) * mm});
            skLineSegment(sketch, "E45.2.0.37", {"start": v(40.7, -1.41) * mm, "end": v(49.65, -10.35) * mm, "construction": true});
            skPoint(sketch, "E45.2.0.38", {"position": v(40, -0.7) * mm});
            skLineSegment(sketch, "E45.2.0.39", {"start": v(40.7, 1.41) * mm, "end": v(49.3, 10) * mm});
            skLineSegment(sketch, "E45.2.0.40", {"start": v(50, -10) * mm, "end": v(49.3, -10) * mm});
            skLineSegment(sketch, "E45.2.0.41", {"start": v(30, 9.3) * mm, "end": v(30, 10) * mm});
            skLineSegment(sketch, "E45.2.0.42", {"start": v(30.7, 10) * mm, "end": v(39.3, 1.41) * mm});
            skLineSegment(sketch, "E45.2.0.43", {"start": v(50, 9.3) * mm, "end": v(41.41, 0.7) * mm});
            skLineSegment(sketch, "E45.2.0.44", {"start": v(30, 10) * mm, "end": v(30.7, 10) * mm});
            skLineSegment(sketch, "E45.2.0.45", {"start": v(49.3, -10) * mm, "end": v(40.7, -1.41) * mm});
            skLineSegment(sketch, "E45.2.0.46", {"start": v(30.7, -10) * mm, "end": v(30, -10) * mm});
            skPoint(sketch, "E45.2.0.47", {"position": v(39.3, 0) * mm});
            skLineSegment(sketch, "E45.2.0.48", {"start": v(50, 10) * mm, "end": v(50, 9.3) * mm});
            skPoint(sketch, "E45.2.0.49", {"position": v(40, 0.7) * mm});
            skLineSegment(sketch, "E45.2.0.50", {"start": v(30, -10) * mm, "end": v(30, -9.3) * mm});
            skLineSegment(sketch, "E45.2.0.51", {"start": v(50, -9.3) * mm, "end": v(50, -10) * mm});
            skLineSegment(sketch, "E45.2.0.52", {"start": v(41.41, -0.7) * mm, "end": v(50, -9.3) * mm});
            skPoint(sketch, "E45.2.0.53", {"position": v(40.7, 0) * mm});
            skLineSegment(sketch, "E45.2.0.54", {"start": v(30, -9.3) * mm, "end": v(38.59, -0.7) * mm});
            skLineSegment(sketch, "E45.2.0.55", {"start": v(38.59, 0.7) * mm, "end": v(30, 9.3) * mm});
            skLineSegment(sketch, "E45.2.0.56", {"start": v(39.3, -1.41) * mm, "end": v(30.7, -10) * mm});
            skLineSegment(sketch, "E45.2.0.57", {"start": v(49.3, 10) * mm, "end": v(50, 10) * mm});
            skPoint(sketch, "E45.2.0.58", {"position": v(39.3, 0) * mm});
            skLineSegment(sketch, "E45.2.1.0", {"start": v(29.65, 29.65) * mm, "end": v(38.59, 20.7) * mm, "construction": true});
            skLineSegment(sketch, "E45.2.1.1", {"start": v(30, 10) * mm, "end": v(50, 30) * mm, "construction": true});
            skLineSegment(sketch, "E45.2.1.2", {"start": v(40, 20.7) * mm, "end": v(40.7, 20) * mm, "construction": true});
            skPoint(sketch, "E45.2.1.3", {"position": v(49.3, 30) * mm});
            skLineSegment(sketch, "E45.2.1.4", {"start": v(50, 10) * mm, "end": v(50, 30) * mm, "construction": true});
            skLineSegment(sketch, "E45.2.1.5", {"start": v(30, 10) * mm, "end": v(30, 30) * mm, "construction": true});
            skArc(sketch, "E45.2.1.6", {"start": v(29.65, 29.65) * mm, "mid": v(29.65, 30.35) * mm, "end": v(30.35, 30.35) * mm, "construction": true});
            skPoint(sketch, "E45.2.1.7", {"position": v(30, 29.3) * mm});
            skArc(sketch, "E45.2.1.8", {"start": v(50.35, 10.35) * mm, "mid": v(50.35, 9.65) * mm, "end": v(49.65, 9.65) * mm, "construction": true});
            skPoint(sketch, "E45.2.1.9", {"position": v(49.3, 10) * mm});
            skPoint(sketch, "E45.2.1.10", {"position": v(50, 29.3) * mm});
            skArc(sketch, "E45.2.1.11", {"start": v(41.41, 20.7) * mm, "mid": v(41.12, 20) * mm, "end": v(41.41, 19.3) * mm});
            skLineSegment(sketch, "E45.2.1.12", {"start": v(41.41, 19.3) * mm, "end": v(50.35, 10.35) * mm, "construction": true});
            skPoint(sketch, "E45.2.1.13", {"position": v(40, 20.7) * mm});
            skLineSegment(sketch, "E45.2.1.14", {"start": v(29.65, 10.35) * mm, "end": v(38.59, 19.3) * mm, "construction": true});
            skPoint(sketch, "E45.2.1.15", {"position": v(30.7, 30) * mm});
            skArc(sketch, "E45.2.1.16", {"start": v(39.3, 21.41) * mm, "mid": v(40, 21.12) * mm, "end": v(40.7, 21.41) * mm});
            skLineSegment(sketch, "E45.2.1.17", {"start": v(40, 19.3) * mm, "end": v(40.7, 20) * mm, "construction": true});
            skLineSegment(sketch, "E45.2.1.18", {"start": v(39.3, 20) * mm, "end": v(40, 20.7) * mm, "construction": true});
            skLineSegment(sketch, "E45.2.1.19", {"start": v(50, 30) * mm, "end": v(30, 30) * mm, "construction": true});
            skPoint(sketch, "E45.2.1.20", {"position": v(40, 20) * mm});
            skLineSegment(sketch, "E45.2.1.21", {"start": v(50, 10) * mm, "end": v(30, 10) * mm, "construction": true});
            skPoint(sketch, "E45.2.1.22", {"position": v(50, 10.7) * mm});
            skLineSegment(sketch, "E45.2.1.23", {"start": v(30.35, 30.35) * mm, "end": v(39.3, 21.41) * mm, "construction": true});
            skLineSegment(sketch, "E45.2.1.24", {"start": v(40.7, 21.41) * mm, "end": v(49.65, 30.35) * mm, "construction": true});
            skLineSegment(sketch, "E45.2.1.25", {"start": v(30, 30) * mm, "end": v(50, 10) * mm, "construction": true});
            skArc(sketch, "E45.2.1.26", {"start": v(30.35, 9.65) * mm, "mid": v(29.65, 9.65) * mm, "end": v(29.65, 10.35) * mm, "construction": true});
            skLineSegment(sketch, "E45.2.1.27", {"start": v(39.3, 20) * mm, "end": v(40, 19.3) * mm, "construction": true});
            skArc(sketch, "E45.2.1.28", {"start": v(49.65, 30.35) * mm, "mid": v(50.35, 30.35) * mm, "end": v(50.35, 29.65) * mm, "construction": true});
            skLineSegment(sketch, "E45.2.1.29", {"start": v(30.35, 9.65) * mm, "end": v(39.3, 18.59) * mm, "construction": true});
            skPoint(sketch, "E45.2.1.30", {"position": v(40.7, 20) * mm});
            skPoint(sketch, "E45.2.1.31", {"position": v(30.7, 10) * mm});
            skArc(sketch, "E45.2.1.32", {"start": v(40.7, 18.59) * mm, "mid": v(40, 18.88) * mm, "end": v(39.3, 18.59) * mm});
            skArc(sketch, "E45.2.1.33", {"start": v(38.59, 19.3) * mm, "mid": v(38.88, 20) * mm, "end": v(38.59, 20.7) * mm});
            skPoint(sketch, "E45.2.1.34", {"position": v(40, 19.3) * mm});
            skLineSegment(sketch, "E45.2.1.35", {"start": v(41.41, 20.7) * mm, "end": v(50.35, 29.65) * mm, "construction": true});
            skPoint(sketch, "E45.2.1.36", {"position": v(30, 10.7) * mm});
            skLineSegment(sketch, "E45.2.1.37", {"start": v(40.7, 18.59) * mm, "end": v(49.65, 9.65) * mm, "construction": true});
            skPoint(sketch, "E45.2.1.38", {"position": v(40, 19.3) * mm});
            skLineSegment(sketch, "E45.2.1.39", {"start": v(40.7, 21.41) * mm, "end": v(49.3, 30) * mm});
            skLineSegment(sketch, "E45.2.1.40", {"start": v(50, 10) * mm, "end": v(49.3, 10) * mm});
            skLineSegment(sketch, "E45.2.1.41", {"start": v(30, 29.3) * mm, "end": v(30, 30) * mm});
            skLineSegment(sketch, "E45.2.1.42", {"start": v(30.7, 30) * mm, "end": v(39.3, 21.41) * mm});
            skLineSegment(sketch, "E45.2.1.43", {"start": v(50, 29.3) * mm, "end": v(41.41, 20.7) * mm});
            skLineSegment(sketch, "E45.2.1.44", {"start": v(30, 30) * mm, "end": v(30.7, 30) * mm});
            skLineSegment(sketch, "E45.2.1.45", {"start": v(49.3, 10) * mm, "end": v(40.7, 18.59) * mm});
            skLineSegment(sketch, "E45.2.1.46", {"start": v(30.7, 10) * mm, "end": v(30, 10) * mm});
            skPoint(sketch, "E45.2.1.47", {"position": v(39.3, 20) * mm});
            skLineSegment(sketch, "E45.2.1.48", {"start": v(50, 30) * mm, "end": v(50, 29.3) * mm});
            skPoint(sketch, "E45.2.1.49", {"position": v(40, 20.7) * mm});
            skLineSegment(sketch, "E45.2.1.50", {"start": v(30, 10) * mm, "end": v(30, 10.7) * mm});
            skLineSegment(sketch, "E45.2.1.51", {"start": v(50, 10.7) * mm, "end": v(50, 10) * mm});
            skLineSegment(sketch, "E45.2.1.52", {"start": v(41.41, 19.3) * mm, "end": v(50, 10.7) * mm});
            skPoint(sketch, "E45.2.1.53", {"position": v(40.7, 20) * mm});
            skLineSegment(sketch, "E45.2.1.54", {"start": v(30, 10.7) * mm, "end": v(38.59, 19.3) * mm});
            skLineSegment(sketch, "E45.2.1.55", {"start": v(38.59, 20.7) * mm, "end": v(30, 29.3) * mm});
            skLineSegment(sketch, "E45.2.1.56", {"start": v(39.3, 18.59) * mm, "end": v(30.7, 10) * mm});
            skLineSegment(sketch, "E45.2.1.57", {"start": v(49.3, 30) * mm, "end": v(50, 30) * mm});
            skPoint(sketch, "E45.2.1.58", {"position": v(39.3, 20) * mm});
            skLineSegment(sketch, "E45.2.2.0", {"start": v(29.65, 49.65) * mm, "end": v(38.59, 40.7) * mm, "construction": true});
            skLineSegment(sketch, "E45.2.2.1", {"start": v(30, 30) * mm, "end": v(50, 50) * mm, "construction": true});
            skLineSegment(sketch, "E45.2.2.2", {"start": v(40, 40.7) * mm, "end": v(40.7, 40) * mm, "construction": true});
            skPoint(sketch, "E45.2.2.3", {"position": v(49.3, 50) * mm});
            skLineSegment(sketch, "E45.2.2.4", {"start": v(50, 30) * mm, "end": v(50, 50) * mm, "construction": true});
            skLineSegment(sketch, "E45.2.2.5", {"start": v(30, 30) * mm, "end": v(30, 50) * mm, "construction": true});
            skArc(sketch, "E45.2.2.6", {"start": v(29.65, 49.65) * mm, "mid": v(29.65, 50.35) * mm, "end": v(30.35, 50.35) * mm, "construction": true});
            skPoint(sketch, "E45.2.2.7", {"position": v(30, 49.3) * mm});
            skArc(sketch, "E45.2.2.8", {"start": v(50.35, 30.35) * mm, "mid": v(50.35, 29.65) * mm, "end": v(49.65, 29.65) * mm, "construction": true});
            skPoint(sketch, "E45.2.2.9", {"position": v(49.3, 30) * mm});
            skPoint(sketch, "E45.2.2.10", {"position": v(50, 49.3) * mm});
            skArc(sketch, "E45.2.2.11", {"start": v(41.41, 40.7) * mm, "mid": v(41.12, 40) * mm, "end": v(41.41, 39.3) * mm});
            skLineSegment(sketch, "E45.2.2.12", {"start": v(41.41, 39.3) * mm, "end": v(50.35, 30.35) * mm, "construction": true});
            skPoint(sketch, "E45.2.2.13", {"position": v(40, 40.7) * mm});
            skLineSegment(sketch, "E45.2.2.14", {"start": v(29.65, 30.35) * mm, "end": v(38.59, 39.3) * mm, "construction": true});
            skPoint(sketch, "E45.2.2.15", {"position": v(30.7, 50) * mm});
            skArc(sketch, "E45.2.2.16", {"start": v(39.3, 41.41) * mm, "mid": v(40, 41.12) * mm, "end": v(40.7, 41.41) * mm});
            skLineSegment(sketch, "E45.2.2.17", {"start": v(40, 39.3) * mm, "end": v(40.7, 40) * mm, "construction": true});
            skLineSegment(sketch, "E45.2.2.18", {"start": v(39.3, 40) * mm, "end": v(40, 40.7) * mm, "construction": true});
            skLineSegment(sketch, "E45.2.2.19", {"start": v(50, 50) * mm, "end": v(30, 50) * mm, "construction": true});
            skPoint(sketch, "E45.2.2.20", {"position": v(40, 40) * mm});
            skLineSegment(sketch, "E45.2.2.21", {"start": v(50, 30) * mm, "end": v(30, 30) * mm, "construction": true});
            skPoint(sketch, "E45.2.2.22", {"position": v(50, 30.7) * mm});
            skLineSegment(sketch, "E45.2.2.23", {"start": v(30.35, 50.35) * mm, "end": v(39.3, 41.41) * mm, "construction": true});
            skLineSegment(sketch, "E45.2.2.24", {"start": v(40.7, 41.41) * mm, "end": v(49.65, 50.35) * mm, "construction": true});
            skLineSegment(sketch, "E45.2.2.25", {"start": v(30, 50) * mm, "end": v(50, 30) * mm, "construction": true});
            skArc(sketch, "E45.2.2.26", {"start": v(30.35, 29.65) * mm, "mid": v(29.65, 29.65) * mm, "end": v(29.65, 30.35) * mm, "construction": true});
            skLineSegment(sketch, "E45.2.2.27", {"start": v(39.3, 40) * mm, "end": v(40, 39.3) * mm, "construction": true});
            skArc(sketch, "E45.2.2.28", {"start": v(49.65, 50.35) * mm, "mid": v(50.35, 50.35) * mm, "end": v(50.35, 49.65) * mm, "construction": true});
            skLineSegment(sketch, "E45.2.2.29", {"start": v(30.35, 29.65) * mm, "end": v(39.3, 38.59) * mm, "construction": true});
            skPoint(sketch, "E45.2.2.30", {"position": v(40.7, 40) * mm});
            skPoint(sketch, "E45.2.2.31", {"position": v(30.7, 30) * mm});
            skArc(sketch, "E45.2.2.32", {"start": v(40.7, 38.59) * mm, "mid": v(40, 38.88) * mm, "end": v(39.3, 38.59) * mm});
            skArc(sketch, "E45.2.2.33", {"start": v(38.59, 39.3) * mm, "mid": v(38.88, 40) * mm, "end": v(38.59, 40.7) * mm});
            skPoint(sketch, "E45.2.2.34", {"position": v(40, 39.3) * mm});
            skLineSegment(sketch, "E45.2.2.35", {"start": v(41.41, 40.7) * mm, "end": v(50.35, 49.65) * mm, "construction": true});
            skPoint(sketch, "E45.2.2.36", {"position": v(30, 30.7) * mm});
            skLineSegment(sketch, "E45.2.2.37", {"start": v(40.7, 38.59) * mm, "end": v(49.65, 29.65) * mm, "construction": true});
            skPoint(sketch, "E45.2.2.38", {"position": v(40, 39.3) * mm});
            skLineSegment(sketch, "E45.2.2.39", {"start": v(40.7, 41.41) * mm, "end": v(49.3, 50) * mm});
            skLineSegment(sketch, "E45.2.2.40", {"start": v(50, 30) * mm, "end": v(49.3, 30) * mm});
            skLineSegment(sketch, "E45.2.2.41", {"start": v(30, 49.3) * mm, "end": v(30, 50) * mm});
            skLineSegment(sketch, "E45.2.2.42", {"start": v(30.7, 50) * mm, "end": v(39.3, 41.41) * mm});
            skLineSegment(sketch, "E45.2.2.43", {"start": v(50, 49.3) * mm, "end": v(41.41, 40.7) * mm});
            skLineSegment(sketch, "E45.2.2.44", {"start": v(30, 50) * mm, "end": v(30.7, 50) * mm});
            skLineSegment(sketch, "E45.2.2.45", {"start": v(49.3, 30) * mm, "end": v(40.7, 38.59) * mm});
            skLineSegment(sketch, "E45.2.2.46", {"start": v(30.7, 30) * mm, "end": v(30, 30) * mm});
            skPoint(sketch, "E45.2.2.47", {"position": v(39.3, 40) * mm});
            skLineSegment(sketch, "E45.2.2.48", {"start": v(50, 50) * mm, "end": v(50, 49.3) * mm});
            skPoint(sketch, "E45.2.2.49", {"position": v(40, 40.7) * mm});
            skLineSegment(sketch, "E45.2.2.50", {"start": v(30, 30) * mm, "end": v(30, 30.7) * mm});
            skLineSegment(sketch, "E45.2.2.51", {"start": v(50, 30.7) * mm, "end": v(50, 30) * mm});
            skLineSegment(sketch, "E45.2.2.52", {"start": v(41.41, 39.3) * mm, "end": v(50, 30.7) * mm});
            skPoint(sketch, "E45.2.2.53", {"position": v(40.7, 40) * mm});
            skLineSegment(sketch, "E45.2.2.54", {"start": v(30, 30.7) * mm, "end": v(38.59, 39.3) * mm});
            skLineSegment(sketch, "E45.2.2.55", {"start": v(38.59, 40.7) * mm, "end": v(30, 49.3) * mm});
            skLineSegment(sketch, "E45.2.2.56", {"start": v(39.3, 38.59) * mm, "end": v(30.7, 30) * mm});
            skLineSegment(sketch, "E45.2.2.57", {"start": v(49.3, 50) * mm, "end": v(50, 50) * mm});
            skPoint(sketch, "E45.2.2.58", {"position": v(39.3, 40) * mm});
            skLineSegment(sketch, "E45.direction1", {"start": v(-9.65, -10.35) * mm, "end": v(10.35, -10.35) * mm, "construction": true});
            skLineSegment(sketch, "E45.direction2", {"start": v(-9.65, -10.35) * mm, "end": v(-9.65, 9.65) * mm, "construction": true});
            skSolve(sketch);
        }
        {
            var Q0;
            Q0=makeQuery(id+"F0.imprint","IMPRINT",FACE,{"disambiguationData":[TD([[makeQuery(id+"F0.imprint","IMPRINT",EDGE,{"derivedFrom":sQuery(id+"F0.wireOp",EDGE,"E17.filletArc")}),-1.0]])]});
            var Q1;
            Q1=makeQuery(id+"F0.imprint","IMPRINT",FACE,{"disambiguationData":[TD([[makeQuery(id+"F0.imprint","IMPRINT",EDGE,{"derivedFrom":sQuery(id+"F0.wireOp",EDGE,"E45.1.1.11")}),-1.0]])]});
            var Q2;
            Q2=makeQuery(id+"F0.imprint","IMPRINT",FACE,{"disambiguationData":[TD([[makeQuery(id+"F0.imprint","IMPRINT",EDGE,{"derivedFrom":sQuery(id+"F0.wireOp",EDGE,"E45.1.0.11")}),-1.0]])]});
            var Q3;
            Q3=makeQuery(id+"F0.imprint","IMPRINT",FACE,{"disambiguationData":[TD([[makeQuery(id+"F0.imprint","IMPRINT",EDGE,{"derivedFrom":sQuery(id+"F0.wireOp",EDGE,"E45.0.1.11")}),-1.0]])]});
            var Q4;
            Q4=makeQuery(id+"F0.imprint","IMPRINT",FACE,{"disambiguationData":[TD([[makeQuery(id+"F0.imprint","IMPRINT",EDGE,{"derivedFrom":sQuery(id+"F0.wireOp",EDGE,"E45.2.1.11")}),-1.0]])]});
            var Q5;
            Q5=makeQuery(id+"F0.imprint","IMPRINT",FACE,{"disambiguationData":[TD([[makeQuery(id+"F0.imprint","IMPRINT",EDGE,{"derivedFrom":sQuery(id+"F0.wireOp",EDGE,"E45.2.0.11")}),-1.0]])]});
            var Q6;
            Q6=makeQuery(id+"F0.imprint","IMPRINT",FACE,{"disambiguationData":[TD([[makeQuery(id+"F0.imprint","IMPRINT",EDGE,{"derivedFrom":sQuery(id+"F0.wireOp",EDGE,"E45.2.2.11")}),-1.0]])]});
            var Q7;
            Q7=makeQuery(id+"F0.imprint","IMPRINT",FACE,{"disambiguationData":[TD([[makeQuery(id+"F0.imprint","IMPRINT",EDGE,{"derivedFrom":sQuery(id+"F0.wireOp",EDGE,"E45.1.2.11")}),-1.0]])]});
            var Q8;
            Q8=makeQuery(id+"F0.imprint","IMPRINT",FACE,{"disambiguationData":[TD([[makeQuery(id+"F0.imprint","IMPRINT",EDGE,{"derivedFrom":sQuery(id+"F0.wireOp",EDGE,"E45.0.2.11")}),-1.0]])]});
            extrude(context, id + "F1", {"entities" : qUnion([Q0, Q1, Q2, Q3, Q4, Q5, Q6, Q7, Q8]), "depth" : 2 * mm, "offsetDistance" : 25 * mm});
        }
        {
            var Q0;
            Q0=makeQuery(id+"F0.imprint","IMPRINT",FACE,{"disambiguationData":[TD([[makeQuery(id+"F0.imprint","IMPRINT",EDGE,{"derivedFrom":sQuery(id+"F0.wireOp",EDGE,"E18.filletArc")}),1.0]])]});
            var Q1;
            Q1=makeQuery(id+"F0.imprint","IMPRINT",FACE,{"disambiguationData":[TD([[makeQuery(id+"F0.imprint","IMPRINT",EDGE,{"derivedFrom":sQuery(id+"F0.wireOp",EDGE,"E19.filletArc")}),1.0]])]});
            var Q2;
            Q2=makeQuery(id+"F0.imprint","IMPRINT",FACE,{"disambiguationData":[TD([[makeQuery(id+"F0.imprint","IMPRINT",EDGE,{"derivedFrom":sQuery(id+"F0.wireOp",EDGE,"E45.0.1.11")}),1.0]])]});
            var Q3;
            Q3=makeQuery(id+"F0.imprint","IMPRINT",FACE,{"disambiguationData":[TD([[makeQuery(id+"F0.imprint","IMPRINT",EDGE,{"derivedFrom":sQuery(id+"F0.wireOp",EDGE,"E45.1.0.16")}),1.0]])]});
            var Q4;
            Q4=makeQuery(id+"F0.imprint","IMPRINT",FACE,{"disambiguationData":[TD([[makeQuery(id+"F0.imprint","IMPRINT",EDGE,{"derivedFrom":sQuery(id+"F0.wireOp",EDGE,"E45.1.0.11")}),1.0]])]});
            var Q5;
            Q5=makeQuery(id+"F0.imprint","IMPRINT",FACE,{"disambiguationData":[TD([[makeQuery(id+"F0.imprint","IMPRINT",EDGE,{"derivedFrom":sQuery(id+"F0.wireOp",EDGE,"E45.1.1.11")}),1.0]])]});
            var Q6;
            Q6=makeQuery(id+"F0.imprint","IMPRINT",FACE,{"disambiguationData":[TD([[makeQuery(id+"F0.imprint","IMPRINT",EDGE,{"derivedFrom":sQuery(id+"F0.wireOp",EDGE,"E45.2.0.16")}),1.0]])]});
            var Q7;
            Q7=makeQuery(id+"F0.imprint","IMPRINT",FACE,{"disambiguationData":[TD([[makeQuery(id+"F0.imprint","IMPRINT",EDGE,{"derivedFrom":sQuery(id+"F0.wireOp",EDGE,"E45.1.1.16")}),1.0]])]});
            var Q8;
            Q8=makeQuery(id+"F0.imprint","IMPRINT",FACE,{"disambiguationData":[TD([[makeQuery(id+"F0.imprint","IMPRINT",EDGE,{"derivedFrom":sQuery(id+"F0.wireOp",EDGE,"E45.0.2.11")}),1.0]])]});
            var Q9;
            Q9=makeQuery(id+"F0.imprint","IMPRINT",FACE,{"disambiguationData":[TD([[makeQuery(id+"F0.imprint","IMPRINT",EDGE,{"derivedFrom":sQuery(id+"F0.wireOp",EDGE,"E45.0.1.16")}),1.0]])]});
            var Q10;
            Q10=makeQuery(id+"F0.imprint","IMPRINT",FACE,{"disambiguationData":[TD([[makeQuery(id+"F0.imprint","IMPRINT",EDGE,{"derivedFrom":sQuery(id+"F0.wireOp",EDGE,"E45.1.2.11")}),1.0]])]});
            var Q11;
            Q11=makeQuery(id+"F0.imprint","IMPRINT",FACE,{"disambiguationData":[TD([[makeQuery(id+"F0.imprint","IMPRINT",EDGE,{"derivedFrom":sQuery(id+"F0.wireOp",EDGE,"E45.2.1.16")}),1.0]])]});
            extrude(context, id + "F2", {"entities" : qUnion([Q0, Q1, Q2, Q3, Q4, Q5, Q6, Q7, Q8, Q9, Q10, Q11]), "operationType" : NewBodyOperationType.ADD, "depth" : 0.4 * mm, "offsetDistance" : 25 * mm});
        }
    });
